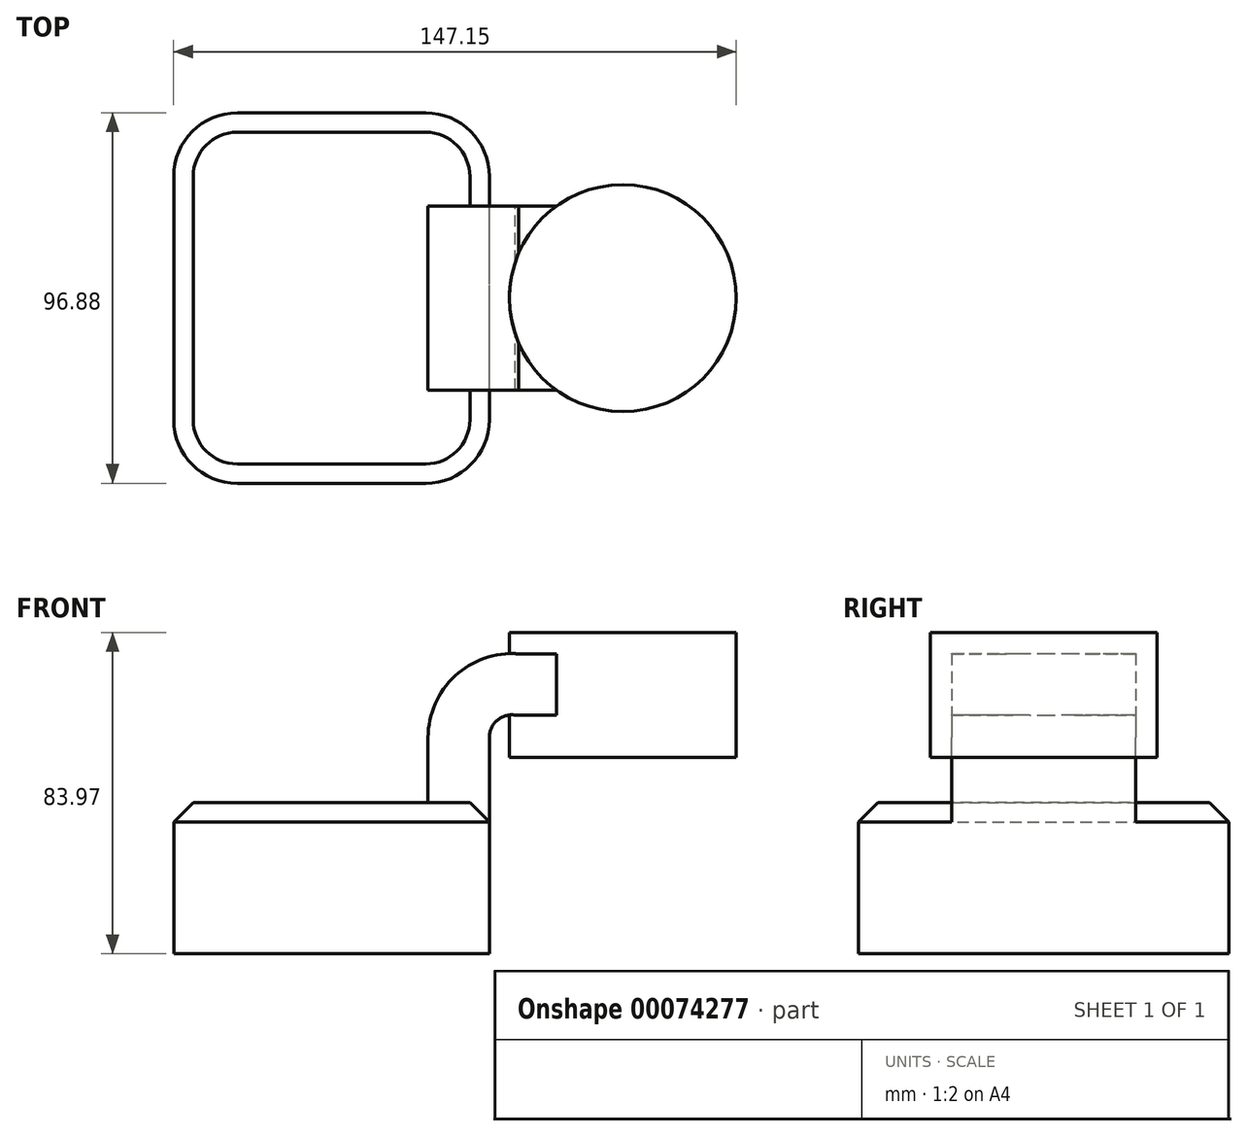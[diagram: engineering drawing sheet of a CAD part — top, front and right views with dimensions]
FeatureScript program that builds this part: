
annotation { "Feature Type Name" : "Feature", "Feature Type Description" : "" }
export const myFeature = defineFeature(function(context is Context, id is Id, definition is map)
    precondition{}
    {
        {
            var Q0;
            Q0=qCreatedBy(makeId("Front.planeOp"),FACE);
            var sketch = newSketch(context, id + "F0", { "sketchPlane" : qUnion([Q0])});
            skLineSegment(sketch, "E0.rect.bottom", {"start": v(41.28, -19.75) * mm, "end": v(-41.28, -19.75) * mm});
            skLineSegment(sketch, "E0.rect.top", {"start": v(41.28, 19.75) * mm, "end": v(-41.28, 19.75) * mm});
            skLineSegment(sketch, "E0.rect.left", {"start": v(41.28, -19.75) * mm, "end": v(41.27, 19.75) * mm});
            skLineSegment(sketch, "E0.rect.right", {"start": v(-41.28, -19.75) * mm, "end": v(-41.28, 19.75) * mm});
            skPoint(sketch, "E0.rect.middle", {"position": v(0, 0) * mm});
            skLineSegment(sketch, "E1.rect.bottom", {"start": v(105.87, 31.62) * mm, "end": v(55.07, 31.62) * mm});
            skLineSegment(sketch, "E1.rect.top", {"start": v(105.87, 64.22) * mm, "end": v(55.07, 64.22) * mm});
            skLineSegment(sketch, "E1.rect.left", {"start": v(105.87, 31.62) * mm, "end": v(105.87, 64.22) * mm});
            skLineSegment(sketch, "E1.rect.right", {"start": v(55.07, 31.62) * mm, "end": v(55.07, 64.22) * mm});
            skPoint(sketch, "E1.rect.middle", {"position": v(80.47, 47.92) * mm});
            skLineSegment(sketch, "E2", {"start": v(41.28, 19.75) * mm, "end": v(41.28, 36.75) * mm});
            skArc(sketch, "E3", {"start": v(41.28, 36.75) * mm, "mid": v(43.34, 41.25) * mm, "end": v(48.1, 42.63) * mm});
            skLineSegment(sketch, "E4", {"start": v(48.1, 42.63) * mm, "end": v(76.2, 42.63) * mm});
            skLineSegment(sketch, "E5.0", {"start": v(48.9, 58.64) * mm, "end": v(76.2, 58.64) * mm});
            skArc(sketch, "E5.1", {"start": v(25.27, 36.75) * mm, "mid": v(32.3, 52.85) * mm, "end": v(48.9, 58.64) * mm});
            skLineSegment(sketch, "E5.2", {"start": v(25.27, 19.75) * mm, "end": v(25.27, 36.75) * mm});
            skLineSegment(sketch, "E6", {"start": v(76.2, 31.62) * mm, "end": v(76.2, 64.22) * mm});
            skFitSpline(sketch, "E7", {"points": [v(-41.28, 19.75) * mm, v(55.07, 58.64) * mm], "startDerivative": vector(-4.6, 136.77) * mm, "endDerivative": vector(-0.6, -38.28) * mm});
            skSolve(sketch);
        }
        {
            var Q0;
            Q0=makeQuery(id+"F0.imprint","IMPRINT",FACE,{"disambiguationData":[TD([[makeQuery(id+"F0.imprint","IMPRINT",EDGE,{"derivedFrom":sQuery(id+"F0.wireOp",EDGE,"E0.rect.bottom")}),-1.0]])]});
            extrude(context, id + "F1", {"entities" : qUnion([Q0]), "endBound" : BoundingType.SYMMETRIC, "depth" : 96.89 * mm});
        }
        {
            var Q0;
            {var subQ1=sQuery(id+"F0.wireOp",EDGE,"E2");Q0=makeQuery(id+"F0.imprint","IMPRINT",FACE,{"disambiguationData":[TD([[makeQuery(id+"F0.imprint","IMPRINT",EDGE,{"derivedFrom":subQ1}),1.0]])]});}
            var Q1;
            {var subQ3=sQuery(id+"F0.wireOp",EDGE,"E4");var subQ5=sQuery(id+"F0.wireOp",EDGE,"E6");var subQ6=makeQuery(id+"F0.imprint","INTERSECT",VERTEX,{"derivedFrom":[subQ3,subQ5]});Q1=makeQuery(id+"F0.imprint","IMPRINT",FACE,{"disambiguationData":[TD([[makeQuery(id+"F0.imprint","IMPRINT",EDGE,{"disambiguationData":[TD([[subQ6,1.0]])],"derivedFrom":subQ3}),1.0]])]});}
            var Q2;
            {var subQ0=sQuery(id+"F0.wireOp",EDGE,"E1.rect.left");Q2=makeQuery(id+"F0.imprint","IMPRINT",FACE,{"disambiguationData":[TD([[makeQuery(id+"F0.imprint","IMPRINT",EDGE,{"derivedFrom":subQ0}),1.0]])]});}
            extrude(context, id + "F2", {"entities" : qUnion([Q0, Q1, Q2]), "operationType" : NewBodyOperationType.ADD, "endBound" : BoundingType.SYMMETRIC, "depth" : 48.1 * mm});
        }
        {
            var Q0;
            {var subQ0=sQuery(id+"F0.wireOp",EDGE,"E5.1");Q0=makeQuery(id+"F0.imprint","IMPRINT",FACE,{"disambiguationData":[TD([[makeQuery(id+"F0.imprint","IMPRINT",EDGE,{"derivedFrom":subQ0}),1.0]])]});}
            var Q1;
            Q1=makeQuery(id+"F2.opExtrude","CAP_FACE",FACE,{"disambiguationData":[OSD([sQuery(id+"F0.wireOp",EDGE,"E0.rect.top"),sQuery(id+"F0.wireOp",EDGE,"E1.rect.bottom"),sQuery(id+"F0.wireOp",EDGE,"E1.rect.top"),sQuery(id+"F0.wireOp",EDGE,"E1.rect.left"),sQuery(id+"F0.wireOp",EDGE,"E2"),sQuery(id+"F0.wireOp",EDGE,"E3"),sQuery(id+"F0.wireOp",EDGE,"E4"),sQuery(id+"F0.wireOp",EDGE,"E5.0"),sQuery(id+"F0.wireOp",EDGE,"E5.1"),sQuery(id+"F0.wireOp",EDGE,"E5.2"),sQuery(id+"F0.wireOp",EDGE,"E6")])],"isStart":true});
            extrude(context, id + "F3", {"entities" : qUnion([Q0]), "operationType" : NewBodyOperationType.ADD, "endBound" : BoundingType.UP_TO_SURFACE, "oppositeDirection" : true, "endBoundEntityFace" : qUnion([Q1]), "depth" : 25.4 * mm});
        }
        {
            var Q0;
            Q0=makeQuery(id+"F2.opExtrude","SWEPT_FACE",FACE,{"disambiguationData":[OSD([sQuery(id+"F0.wireOp",EDGE,"E1.rect.left")])]});
            extrude(context, id + "F4", {"entities" : qUnion([Q0]), "operationType" : NewBodyOperationType.ADD, "oppositeDirection" : true, "depth" : 15.5 * mm});
        }
        {
            var Q0;
            Q0=makeQuery(id+"F2.opExtrude","SWEPT_FACE",FACE,{"disambiguationData":[OSD([sQuery(id+"F0.wireOp",EDGE,"E1.rect.left")])]});
            extrude(context, id + "F5", {"entities" : qUnion([Q0]), "operationType" : NewBodyOperationType.REMOVE, "oppositeDirection" : true, "depth" : 16.86 * mm});
        }
        {
            var Q0;
            {var subQ0=sQuery(id+"F0.wireOp",EDGE,"E1.rect.left");Q0=makeQuery(id+"F0.imprint","IMPRINT",FACE,{"disambiguationData":[TD([[makeQuery(id+"F0.imprint","IMPRINT",EDGE,{"derivedFrom":subQ0}),1.0]])]});}
            var Q1;
            Q1=sQuery(id+"F0.wireOp",EDGE,"E6");
            revolve(context, id + "F6", {"operationType" : NewBodyOperationType.ADD, "entities" : qUnion([Q0]), "axis" : qUnion([Q1]), "revolveType" : RevolveType.FULL});
        }
        {
            var Q0;
            Q0=makeQuery(id+"F1.opExtrude","CAP_EDGE",EDGE,{"disambiguationData":[OSD([sQuery(id+"F0.wireOp",EDGE,"E0.rect.right")])],"isStart":false});
            var Q1;
            Q1=makeQuery(id+"F1.opExtrude","CAP_EDGE",EDGE,{"disambiguationData":[OSD([sQuery(id+"F0.wireOp",EDGE,"E0.rect.left")])],"isStart":false});
            var Q2;
            Q2=makeQuery(id+"F1.opExtrude","CAP_EDGE",EDGE,{"disambiguationData":[OSD([sQuery(id+"F0.wireOp",EDGE,"E0.rect.left")])],"isStart":true});
            var Q3;
            Q3=makeQuery(id+"F1.opExtrude","CAP_EDGE",EDGE,{"disambiguationData":[OSD([sQuery(id+"F0.wireOp",EDGE,"E0.rect.right")])],"isStart":true});
            fillet(context, id + "F7", {"entities" : qUnion([Q0, Q1, Q2, Q3]), "radius" : 16.64 * mm, "tangentPropagation" : true, "allowEdgeOverflow" : false});
        }
        {
            var Q0;
            Q0=makeQuery(id+"F1.opExtrude","CAP_EDGE",EDGE,{"disambiguationData":[OSD([sQuery(id+"F0.wireOp",EDGE,"E0.rect.top")])],"isStart":true});
            var Q1;
            Q1=makeQuery(id+"F1.opExtrude","CAP_EDGE",EDGE,{"disambiguationData":[OSD([sQuery(id+"F0.wireOp",EDGE,"E0.rect.top")])],"isStart":false});
            chamfer(context, id + "F8", {"entities" : qUnion([Q0, Q1]), "width" : 5.08 * mm, "tangentPropagation" : true});
        }
    });
